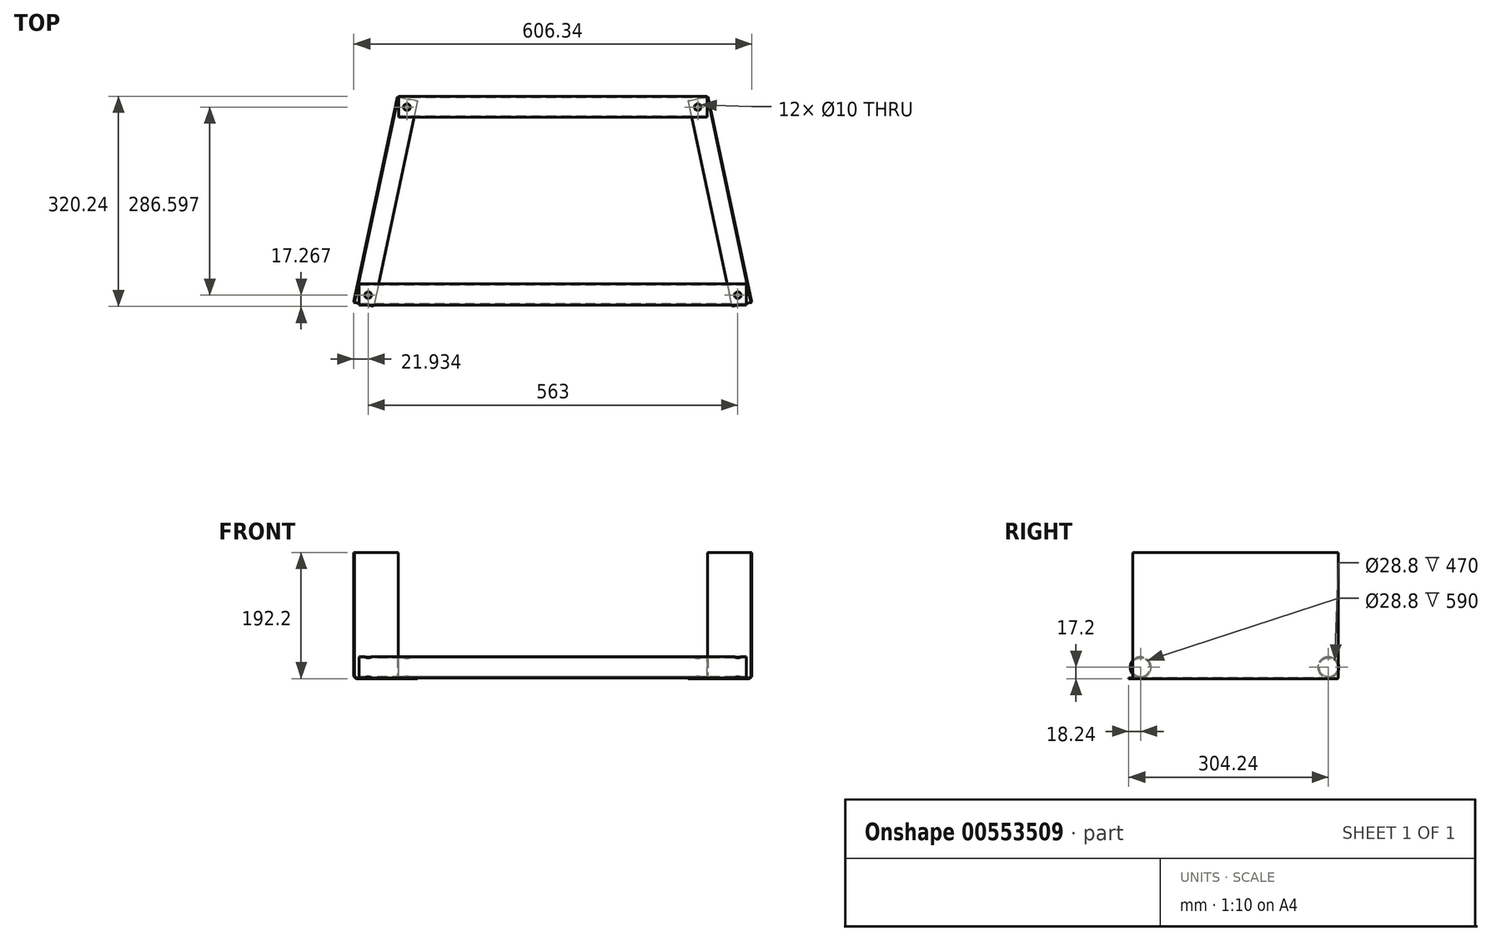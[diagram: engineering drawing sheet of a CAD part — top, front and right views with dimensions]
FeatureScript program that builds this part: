
annotation { "Feature Type Name" : "Feature", "Feature Type Description" : "" }
export const myFeature = defineFeature(function(context is Context, id is Id, definition is map)
    precondition{}
    {
        {
            var Q0;
            Q0=qCreatedBy(makeId("Right.planeOp"),FACE);
            var sketch = newSketch(context, id + "F0", { "sketchPlane" : qUnion([Q0])});
            skCircle(sketch, "E0", {"center": v(-143, 0) * mm, "radius": 16 * mm});
            skCircle(sketch, "E1.0", {"center": v(-143, 0) * mm, "radius": 14.4 * mm});
            skSolve(sketch);
        }
        {
            var Q0;
            Q0=qSketchRegion(id+"F0",true);
            extrude(context, id + "F1", {"entities" : qUnion([Q0]), "depth" : 590 * mm, "offsetDistance" : 25 * mm, "hasSecondDirection" : true, "secondDirectionOppositeDirection" : true, "secondDirectionDepth" : 283 * mm, "symmetric" : true});
        }
        {
            var Q0;
            Q0=qCreatedBy(makeId("Right.planeOp"),FACE);
            var sketch = newSketch(context, id + "F2", { "sketchPlane" : qUnion([Q0])});
            skCircle(sketch, "E2", {"center": v(143, 0) * mm, "radius": 16 * mm});
            skCircle(sketch, "E3.0", {"center": v(143, 0) * mm, "radius": 14.4 * mm});
            skSolve(sketch);
        }
        {
            var Q0;
            Q0=qSketchRegion(id+"F2",true);
            extrude(context, id + "F3", {"entities" : qUnion([Q0]), "depth" : 470 * mm, "offsetDistance" : 25 * mm, "hasSecondDirection" : true, "secondDirectionOppositeDirection" : true, "secondDirectionDepth" : 223 * mm, "symmetric" : true});
        }
        {
            var Q0;
            Q0=qCreatedBy(makeId("Top.planeOp"),FACE);
            var sketch = newSketch(context, id + "F4", { "sketchPlane" : qUnion([Q0])});
            skLineSegment(sketch, "E4", {"start": v(302, -155) * mm, "end": v(235.47, 158) * mm});
            skLineSegment(sketch, "E5.0", {"start": v(303.17, -154.76) * mm, "end": v(236.64, 158.25) * mm});
            skLineSegment(sketch, "E6", {"start": v(235.47, 158) * mm, "end": v(236.64, 158.25) * mm});
            skLineSegment(sketch, "E7", {"start": v(302, -155) * mm, "end": v(303.17, -154.76) * mm});
            skSolve(sketch);
        }
        {
            var Q0;
            Q0=qSketchRegion(id+"F4",true);
            extrude(context, id + "F5", {"entities" : qUnion([Q0]), "depth" : 175 * mm, "offsetDistance" : 25 * mm});
        }
        {
            var Q0;
            Q0=makeQuery(id+"F5.opExtrude","SWEPT_FACE",FACE,{"disambiguationData":[OSD([sQuery(id+"F4.wireOp",EDGE,"E7")])]});
            var sketch = newSketch(context, id + "F6", { "sketchPlane" : qUnion([Q0])});
            skLineSegment(sketch, "E8", {"start": v(263.17, 0) * mm, "end": v(263.17, -12) * mm});
            skLineSegment(sketch, "E9", {"start": v(259.17, -16) * mm, "end": v(233.17, -16) * mm});
            skLineSegment(sketch, "E10", {"start": v(233.17, -16) * mm, "end": v(233.17, -17.2) * mm});
            skLineSegment(sketch, "E11", {"start": v(233.17, -17.2) * mm, "end": v(259.37, -17.2) * mm});
            skLineSegment(sketch, "E12", {"start": v(264.37, -12.2) * mm, "end": v(264.37, 0) * mm});
            skLineSegment(sketch, "E13", {"start": v(264.37, 0) * mm, "end": v(263.17, 0) * mm});
            skPoint(sketch, "E14.visualSharp", {"position": v(263.17, -16) * mm});
            skArc(sketch, "E14.filletArc", {"start": v(259.17, -16) * mm, "mid": v(262, -14.83) * mm, "end": v(263.17, -12) * mm});
            skPoint(sketch, "E15.visualSharp", {"position": v(264.37, -17.2) * mm});
            skArc(sketch, "E15.filletArc", {"start": v(259.37, -17.2) * mm, "mid": v(262.9, -15.74) * mm, "end": v(264.37, -12.2) * mm});
            skSolve(sketch);
        }
        {
            var Q0;
            Q0=qSketchRegion(id+"F6",true);
            extrude(context, id + "F7", {"entities" : qUnion([Q0]), "operationType" : NewBodyOperationType.ADD, "oppositeDirection" : true, "depth" : 320 * mm, "offsetDistance" : 25 * mm});
        }
        {
            var Q0;
            Q0=makeQuery(id+"F5.opExtrude","SWEPT_BODY",BODY,{"disambiguationData":[OSD([sQuery(id+"F4.wireOp",EDGE,"E4"),sQuery(id+"F4.wireOp",EDGE,"E5.0"),sQuery(id+"F4.wireOp",EDGE,"E6"),sQuery(id+"F4.wireOp",EDGE,"E7")])]});
            var Q1;
            Q1=qCreatedBy(makeId("Right.planeOp"),FACE);
            mirror(context, id + "F8", {"entities" : qUnion([Q0]), "mirrorPlane" : qUnion([Q1])});
        }
        {
            var Q0;
            Q0=makeQuery(id+"F8.opPattern","COPY",FACE,{"derivedFrom":makeQuery(id+"F7.opExtrude","SWEPT_FACE",FACE,{"disambiguationData":[OSD([sQuery(id+"F6.wireOp",EDGE,"E11")])]}),"instanceName":"1"});
            var sketch = newSketch(context, id + "F9", { "sketchPlane" : qUnion([Q0])});
            skCircle(sketch, "E16", {"center": v(281.76, 143.97) * mm, "radius": 5 * mm});
            skCircle(sketch, "E17.1.0.0", {"center": v(-281.24, 143.97) * mm, "radius": 5 * mm});
            skLineSegment(sketch, "E17.direction1", {"start": v(281.76, 143.97) * mm, "end": v(-281.24, 143.97) * mm, "construction": true});
            skCircle(sketch, "E18", {"center": v(220.85, -142.62) * mm, "radius": 5 * mm});
            skCircle(sketch, "E19.1.0.0", {"center": v(-222.15, -142.62) * mm, "radius": 5 * mm});
            skLineSegment(sketch, "E19.direction1", {"start": v(220.85, -142.62) * mm, "end": v(-222.15, -142.62) * mm, "construction": true});
            skSolve(sketch);
        }
        {
            var Q0;
            Q0=qSketchRegion(id+"F9",true);
            extrude(context, id + "F10", {"entities" : qUnion([Q0]), "operationType" : NewBodyOperationType.REMOVE, "oppositeDirection" : true, "depth" : 34 * mm, "offsetDistance" : 25 * mm});
        }
        {
            var Q0;
            Q0=qCreatedBy(makeId("Top.planeOp"),FACE);
            cPlane(context, id + "F11", {"entities" : qUnion([Q0]), "cplaneType" : CPlaneType.OFFSET, "offset" : 16 * mm, "width" : 150 * mm, "height" : 150 * mm});
        }
        {
            var Q0;
            Q0=qCreatedBy(id+"F11.planeOp",FACE);
            var sketch = newSketch(context, id + "F12", { "sketchPlane" : qUnion([Q0])});
            skLineSegment(sketch, "E20", {"start": v(-203.78, 159) * mm, "end": v(203.78, 159) * mm});
            skLineSegment(sketch, "E21", {"start": v(270.94, -159) * mm, "end": v(-270.94, -159) * mm});
            skLineSegment(sketch, "E22.0", {"start": v(-204.75, 158.2) * mm, "end": v(-271.92, -157.8) * mm});
            skLineSegment(sketch, "E23.0", {"start": v(204.75, 158.2) * mm, "end": v(271.92, -157.8) * mm});
            skPoint(sketch, "E24.newPointA", {"position": v(-206.12, 151.76) * mm});
            skArc(sketch, "E24.filletArc", {"start": v(-203.78, 159) * mm, "mid": v(-204.4, 158.78) * mm, "end": v(-204.75, 158.2) * mm});
            skPoint(sketch, "E25.newPointA", {"position": v(206.12, 151.76) * mm});
            skArc(sketch, "E25.filletArc", {"start": v(204.75, 158.2) * mm, "mid": v(204.4, 158.78) * mm, "end": v(203.78, 159) * mm});
            skPoint(sketch, "E26.newPointA", {"position": v(-272.66, -161.24) * mm});
            skArc(sketch, "E26.filletArc", {"start": v(-271.92, -157.8) * mm, "mid": v(-271.72, -158.63) * mm, "end": v(-270.94, -159) * mm});
            skPoint(sketch, "E27.newPointA", {"position": v(272.66, -161.24) * mm});
            skArc(sketch, "E27.filletArc", {"start": v(270.94, -159) * mm, "mid": v(271.72, -158.63) * mm, "end": v(271.92, -157.8) * mm});
            skSolve(sketch);
        }
        {
            var Q0;
            Q0 = qSketchRegion(id + "F12", true);
            extrude(context, id + "F13", {"entities" : qUnion([Q0]), "operationType" : NewBodyOperationType.ADD, "depth" : 1 * mm, "offsetDistance" : 25 * mm});
        }
        {
            var Q0;
            Q0=makeQuery(id+"F13.opExtrude","SWEPT_BODY",BODY,{"disambiguationData":[OSD([sQuery(id+"F12.wireOp",EDGE,"E20"),sQuery(id+"F12.wireOp",EDGE,"E21"),sQuery(id+"F12.wireOp",EDGE,"E22.0"),sQuery(id+"F12.wireOp",EDGE,"E23.0"),sQuery(id+"F12.wireOp",EDGE,"E24.filletArc"),sQuery(id+"F12.wireOp",EDGE,"E25.filletArc"),sQuery(id+"F12.wireOp",EDGE,"E26.filletArc"),sQuery(id+"F12.wireOp",EDGE,"E27.filletArc")])]});
            deleteBodies(context, id + "F14", {"entities" : qUnion([Q0])});
        }
    });
